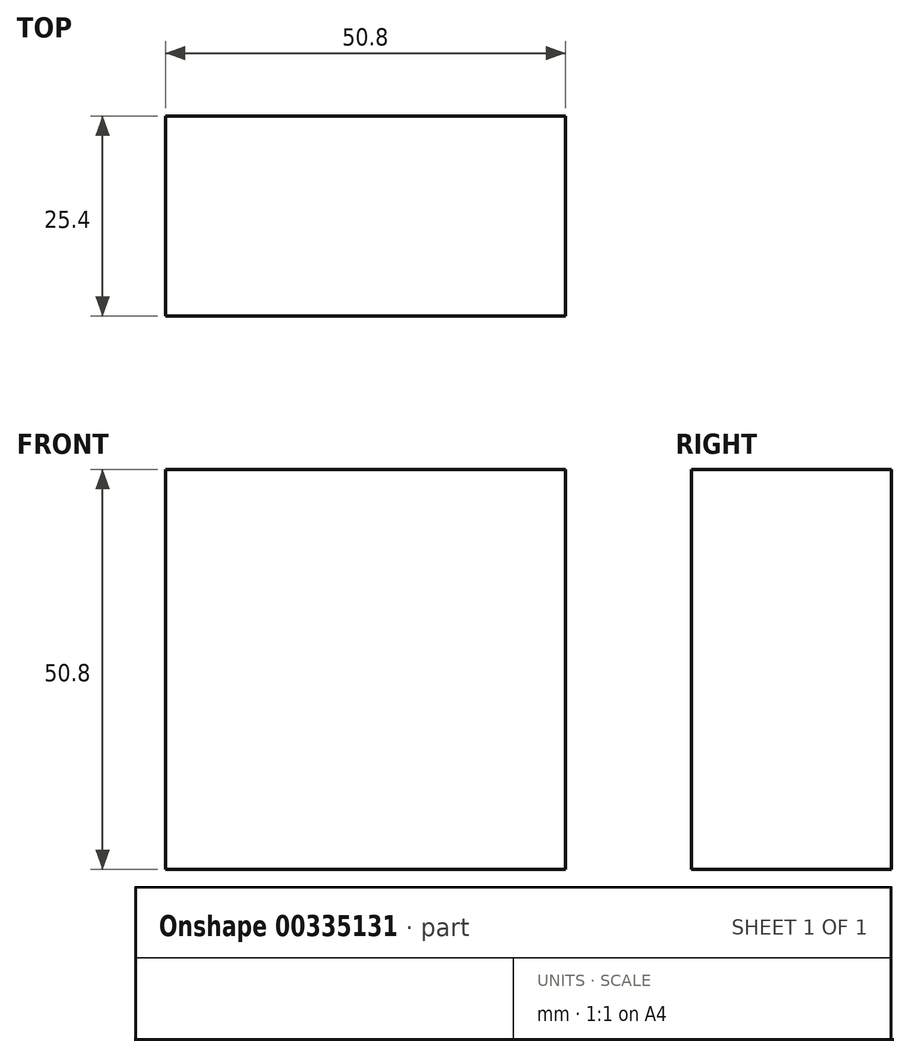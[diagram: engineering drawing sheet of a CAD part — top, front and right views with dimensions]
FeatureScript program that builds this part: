
annotation { "Feature Type Name" : "Feature", "Feature Type Description" : "" }
export const myFeature = defineFeature(function(context is Context, id is Id, definition is map)
    precondition{}
    {
        {
            var Q0;
            Q0=qCreatedBy(makeId("Front.planeOp"),FACE);
            var sketch = newSketch(context, id + "F0", { "sketchPlane" : qUnion([Q0])});
            skLineSegment(sketch, "E0.bottom", {"start": v(-12.65, 5) * mm, "end": v(-63.45, 5) * mm});
            skLineSegment(sketch, "E0.top", {"start": v(-12.65, -45.8) * mm, "end": v(-63.45, -45.8) * mm});
            skLineSegment(sketch, "E0.left", {"start": v(-12.65, 5) * mm, "end": v(-12.65, -45.8) * mm});
            skLineSegment(sketch, "E0.right", {"start": v(-63.45, 5) * mm, "end": v(-63.45, -45.8) * mm});
            skSolve(sketch);
        }
        {
            var Q0;
            Q0 = qSketchRegion(id + "F0", true);
            extrude(context, id + "F1", {"entities" : qUnion([Q0]), "depth" : 25.4 * mm});
        }
    });
